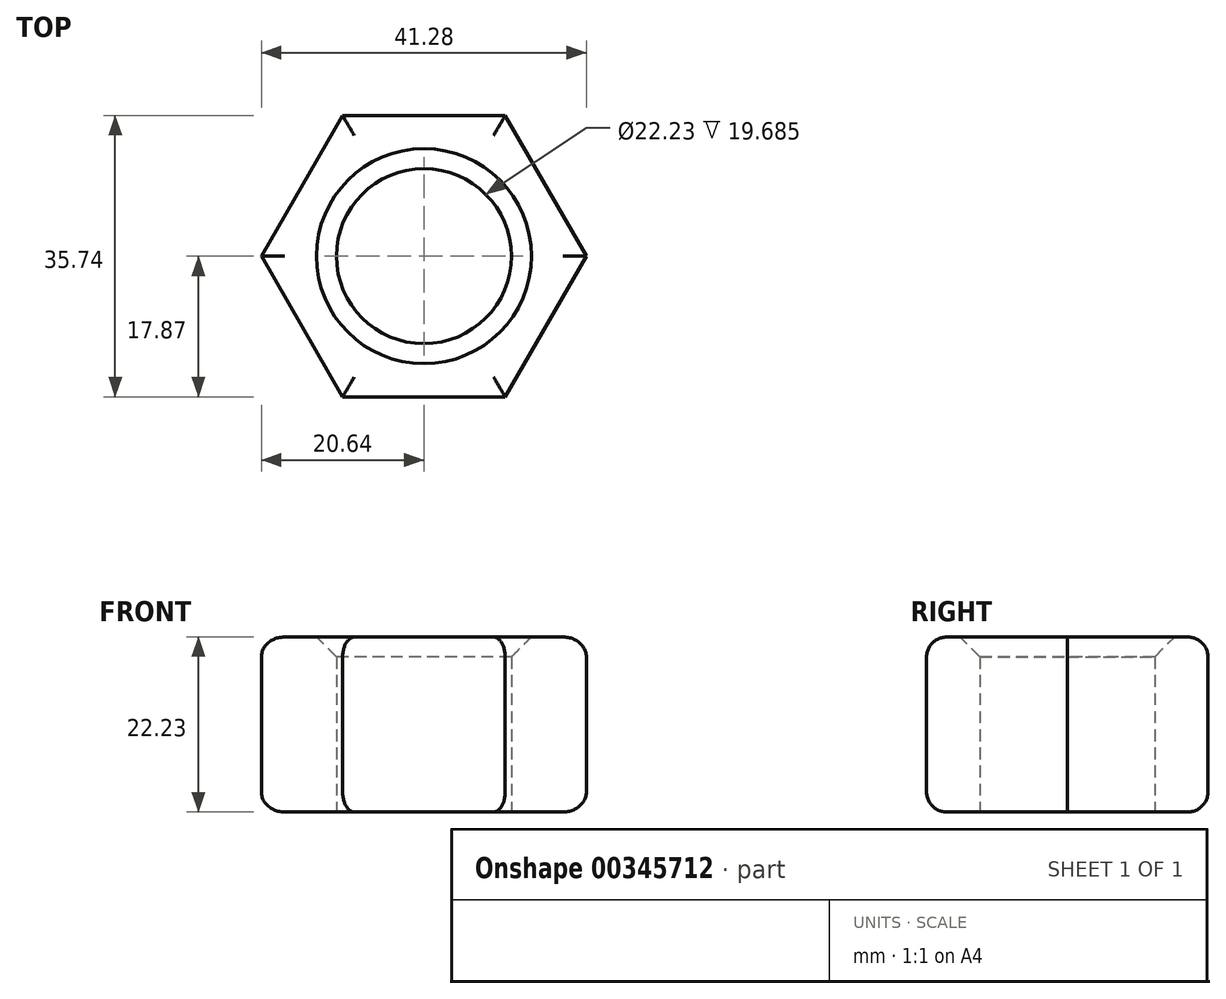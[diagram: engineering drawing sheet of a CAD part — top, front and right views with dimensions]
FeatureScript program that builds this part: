
annotation { "Feature Type Name" : "Feature", "Feature Type Description" : "" }
export const myFeature = defineFeature(function(context is Context, id is Id, definition is map)
    precondition{}
    {
        {
            var Q0;
            Q0=qCreatedBy(makeId("Top.planeOp"),FACE);
            var sketch = newSketch(context, id + "F0", { "sketchPlane" : qUnion([Q0])});
            skCircle(sketch, "E0.cCircle", {"center": v(0, 0) * mm, "radius": 20.64 * mm, "construction": true});
            skLineSegment(sketch, "E0.0", {"start": v(20.64, 0) * mm, "end": v(10.32, -17.87) * mm});
            skLineSegment(sketch, "E0.1", {"start": v(10.32, -17.87) * mm, "end": v(-10.32, -17.87) * mm});
            skLineSegment(sketch, "E0.2", {"start": v(-10.32, -17.87) * mm, "end": v(-20.64, 0) * mm});
            skLineSegment(sketch, "E0.3", {"start": v(-20.64, 0) * mm, "end": v(-10.32, 17.87) * mm});
            skLineSegment(sketch, "E0.4", {"start": v(-10.32, 17.87) * mm, "end": v(10.32, 17.87) * mm});
            skLineSegment(sketch, "E0.5", {"start": v(10.32, 17.87) * mm, "end": v(20.64, 0) * mm});
            skCircle(sketch, "E1", {"center": v(0, 0) * mm, "radius": 11.11 * mm});
            skSolve(sketch);
        }
        {
            var Q0;
            Q0=makeQuery(id+"F0.imprint","IMPRINT",FACE,{"disambiguationData":[TD([[makeQuery(id+"F0.imprint","IMPRINT",EDGE,{"derivedFrom":sQuery(id+"F0.wireOp",EDGE,"E0.0")}),-1.0]])]});
            extrude(context, id + "F1", {"entities" : qUnion([Q0]), "depth" : 22.22 * mm});
        }
        {
            var Q0;
            Q0=makeQuery(id+"F1.opExtrude","CAP_EDGE",EDGE,{"disambiguationData":[OSD([sQuery(id+"F0.wireOp",EDGE,"E0.1")])],"isStart":false});
            var Q1;
            Q1=makeQuery(id+"F1.opExtrude","CAP_EDGE",EDGE,{"disambiguationData":[OSD([sQuery(id+"F0.wireOp",EDGE,"E0.0")])],"isStart":false});
            var Q2;
            Q2=makeQuery(id+"F1.opExtrude","CAP_EDGE",EDGE,{"disambiguationData":[OSD([sQuery(id+"F0.wireOp",EDGE,"E0.5")])],"isStart":false});
            var Q3;
            Q3=makeQuery(id+"F1.opExtrude","CAP_EDGE",EDGE,{"disambiguationData":[OSD([sQuery(id+"F0.wireOp",EDGE,"E0.4")])],"isStart":false});
            var Q4;
            Q4=makeQuery(id+"F1.opExtrude","CAP_EDGE",EDGE,{"disambiguationData":[OSD([sQuery(id+"F0.wireOp",EDGE,"E0.3")])],"isStart":false});
            var Q5;
            Q5=makeQuery(id+"F1.opExtrude","CAP_EDGE",EDGE,{"disambiguationData":[OSD([sQuery(id+"F0.wireOp",EDGE,"E0.2")])],"isStart":false});
            var Q6;
            Q6=makeQuery(id+"F1.opExtrude","CAP_EDGE",EDGE,{"disambiguationData":[OSD([sQuery(id+"F0.wireOp",EDGE,"E0.1")])],"isStart":true});
            var Q7;
            Q7=makeQuery(id+"F1.opExtrude","CAP_EDGE",EDGE,{"disambiguationData":[OSD([sQuery(id+"F0.wireOp",EDGE,"E0.2")])],"isStart":true});
            var Q8;
            Q8=makeQuery(id+"F1.opExtrude","CAP_EDGE",EDGE,{"disambiguationData":[OSD([sQuery(id+"F0.wireOp",EDGE,"E0.3")])],"isStart":true});
            var Q9;
            Q9=makeQuery(id+"F1.opExtrude","CAP_EDGE",EDGE,{"disambiguationData":[OSD([sQuery(id+"F0.wireOp",EDGE,"E0.4")])],"isStart":true});
            var Q10;
            Q10=makeQuery(id+"F1.opExtrude","CAP_EDGE",EDGE,{"disambiguationData":[OSD([sQuery(id+"F0.wireOp",EDGE,"E0.5")])],"isStart":true});
            var Q11;
            Q11=makeQuery(id+"F1.opExtrude","CAP_EDGE",EDGE,{"disambiguationData":[OSD([sQuery(id+"F0.wireOp",EDGE,"E0.0")])],"isStart":true});
            fillet(context, id + "F2", {"entities" : qUnion([Q0, Q1, Q2, Q3, Q4, Q5, Q6, Q7, Q8, Q9, Q10, Q11]), "radius" : 2.54 * mm, "tangentPropagation" : true, "allowEdgeOverflow" : false});
        }
        {
            var Q0;
            Q0=makeQuery(id+"F1.opExtrude","CAP_EDGE",EDGE,{"disambiguationData":[OSD([sQuery(id+"F0.wireOp",EDGE,"E1")])],"isStart":false});
            chamfer(context, id + "F3", {"entities" : qUnion([Q0]), "width" : 2.54 * mm, "tangentPropagation" : true});
        }
    });
